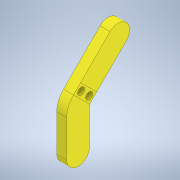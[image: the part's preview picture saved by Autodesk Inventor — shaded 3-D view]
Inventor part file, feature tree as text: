
AUTODESK INVENTOR PART (.ipt)
format: ipt  version: 2020 (Build 240168000, 168)  size: 670,208 bytes
history: native  units: mm
features: sketch x25, extrude x21, reference x11, other x11, projected_geometry x5, plane x4, hole x4, split x2, boolean_combine x2, fillet x2, revolve x1, imported_body x1
ambient origin geometry x8: Origin, YZ Plane, XZ Plane, XY Plane, X Axis, Y Axis, Z Axis, Center Point
bodies: Solid1 (feature_tree), Solid2 (feature_tree), Solid3 (feature_tree), Solid4 (feature_tree), Solid5 (feature_tree), Solid6 (feature_tree)
feature tree (89):
  extrude  "Extrusion1"  Depth=70.0mm
  plane  "Work Plane1"
  extrude  "Extrusion2"  Depth=18.0mm
  extrude  "Extrusion3"  Depth=51.1mm TaperAngle=0.0deg
  extrude  "Extrusion4"  TaperAngle=0.0deg  [1 undecoded]
  extrude  "Extrusion5"  Depth=50.1mm TaperAngle=0.0deg
  extrude  "Extrusion12"  Depth=3.599976mm
  extrude  "Extrusion13"  Depth=0.15mm
  extrude  "Extrusion14"  Depth=0.15mm
  extrude  "Extrusion15"  Depth=5.4mm TaperAngle=0.0deg
  extrude  "Extrusion16"  Depth=3.85mm
  extrude  "Extrusion17"  Depth=53.0mm
  extrude  "Extrusion18"  Depth=37.3mm
  plane  "Work Plane2"
  extrude  "Extrusion19"  Depth=0.15mm
  hole  "Hole1"  [1 undecoded]
  hole  "Hole2"  [1 undecoded]
  plane  "Work Plane3"
  split  "Split1"
  extrude  "Extrusion20"  Depth=8.0mm
  extrude  "Extrusion21"  Depth=45.2mm TaperAngle=0.0deg
  extrude  "Extrusion22"  Depth=12.7mm
  extrude  "Extrusion23"  Depth=12.7mm
  extrude  "Extrusion24"  Depth=18.0mm
  extrude  "Extrusion25"  Depth=9.0mm
  plane  "Work Plane4"
  boolean_combine  "Combine1"
  split  "Split2"
  revolve  "Revolution1"  [1 undecoded]
  imported_body  "Base1"
  boolean_combine  "Combine2"
  fillet  "Fillet1"  Radius=23.3mm
  fillet  "Fillet2"  Radius=17.35mm
  hole  "Hole4"  [1 undecoded]
  extrude  "Extrusion30"  Depth=10.0mm TaperAngle=0.0deg
  extrude  "Extrusion31"  Depth=2.0mm
  sketch  "Sketch1"  dims[d0=18.0mm d1=70.0mm]
  reference  "Reference1"
  sketch  "Sketch2"  dims[d2=70.0mm d3=18.0mm]
  reference  "Reference2"
  sketch  "Sketch3"  dims[d4=18.0mm d5=51.1mm d6=2.0mm d7=0.0mm d8=0.0mm]
  reference  "Reference3"
  reference  "Reference4"
  reference  "Reference5"
  reference  "Reference6"
  reference  "Reference7"
  reference  "Reference8"
  sketch  "Sketch4"  dims[d9=37.3mm d10=0.0mm]
  sketch  "Sketch5"  dims[d11=35.0mm d12=50.1mm d13=0.0mm]
  sketch  "Sketch12"  dims[d14=7.199887mm d15=3.599976mm]
  sketch  "Sketch14"  dims[d16=0.15mm d17=0.15mm]
  reference  "Reference12"
  reference  "Reference13"
  sketch  "Sketch15"  dims[d18=0.15mm d19=0.15mm]
  sketch  "Sketch16"  dims[d20=5.4mm d21=0.0mm d22=15.9mm d23=0.0mm]
  reference  "Reference14"
  sketch  "Sketch17"  dims[d24=5.0mm d25=0.0mm d78=3.85mm]
  sketch  "Sketch19"  dims[d79=10.925mm d80=53.0mm]
  sketch  "Sketch22"  dims[d81=53.0mm d82=37.3mm]
  projected_geometry  "Projected Loop1"
  sketch  "Sketch23"  dims[d83=40.0mm d84=0.0mm d86=0.15mm]
  sketch  "Sketch24"  dims[d87=0.15mm d88=4.0mm d89=0.0mm]
  sketch  "Sketch25"  dims[d90=20.0mm d91=0.0mm d92=10.0mm]
  sketch  "Sketch26"  dims[d93=4.0mm d94=0.0mm d95=8.0mm]
  sketch  "Sketch27"  dims[d96=18.0mm d97=45.2mm d98=0.0mm]
  sketch  "Sketch28"  dims[d99=12.7mm d100=0.3mm]
  sketch  "Sketch29"  dims[d101=12.7mm d102=0.3mm]
  sketch  "Sketch30"  dims[d103=10.0mm d104=0.0mm d109=18.0mm]
  sketch  "Sketch31"  dims[d111=31.0mm d112=9.0mm]
  sketch  "Sketch32"  dims[d113=9.0mm d114=23.3mm d115=23.3mm d116=17.35mm d117=0.0mm]
  projected_geometry  "Projected Loop2"
  projected_geometry  "Projected Loop3"
  sketch  "Sketch33"  dims[d118=15.0mm d119=4.0mm]
  hole  "Hole3"  [1 undecoded]
  sketch  "Sketch39"  dims[d120=8.0mm d121=10.0mm d122=0.0mm]
  projected_geometry  "Projected Loop15"
  sketch  "Sketch40"  dims[d123=3.0mm d124=6.0mm d125=4.0mm d126=2.0mm d127=90.0deg d128=25.75mm d129=0.0mm d132=3.0mm d133=3.0mm d134=4.5mm d135=4.5mm d136=4.0mm d137=4.0mm d138=3.0mm d139=6.0mm d140=4.0mm d141=2.0mm d142=90.0deg d143=56.75mm d144=0.0mm d146=0.765mm d147=1.6mm d148=0.0mm d149=1.6mm d150=0.0mm d151=0.765mm d152=1.7mm d153=0.0mm d154=3.1mm d155=3.1mm d156=2.4mm d157=0.0mm d159=2.4mm d160=0.0mm d162=2.4mm d163=0.0mm d164=3.1mm d166=3.1mm d167=45.0deg d168=2.0mm d169=2.0mm d170=3.4mm d171=6.0mm d172=4.0mm d173=2.0mm d174=90.0deg d175=8.0mm d176=0.0mm d234=63.31207mm d235=25.671847mm d236=110.0mm d237=0.0mm d238=5.6mm d239=5.6mm d240=2.0mm d241=0.0mm d30=0.5mm d31=0.872665mm d32=0.5mm d33=0.872665mm d34=0.872665mm d35=0.5mm d36=0.872665mm]
  projected_geometry  "Projected Loop16"
  parser-record x3  (decoder bookkeeping rows leaked as tree rows — omitted from the tree; the rows remain in map.json)
  other  "Demo2.0004.iam"
  other  "Bearing:2"
  other  "Rolling bearing GB/T 7218-1995 Type FSN 70000-Z F 623-Z:1"
  other  "servo horn 1:1"
  other  "Assembly4.iam"
  other  "Tower Pro MG90S Micro servo:3"
  other  "Крышка корпуса:1"
  other  "Вал последний с чем то:1"
note: 6 required parameter values undecoded (feature->parameter linkage not recoverable at this tier; creation-order binding heuristic only, values carry confidence <= 0.55)
note: 3 file-system paths scrubbed to <path> (originals preserved in map.json)